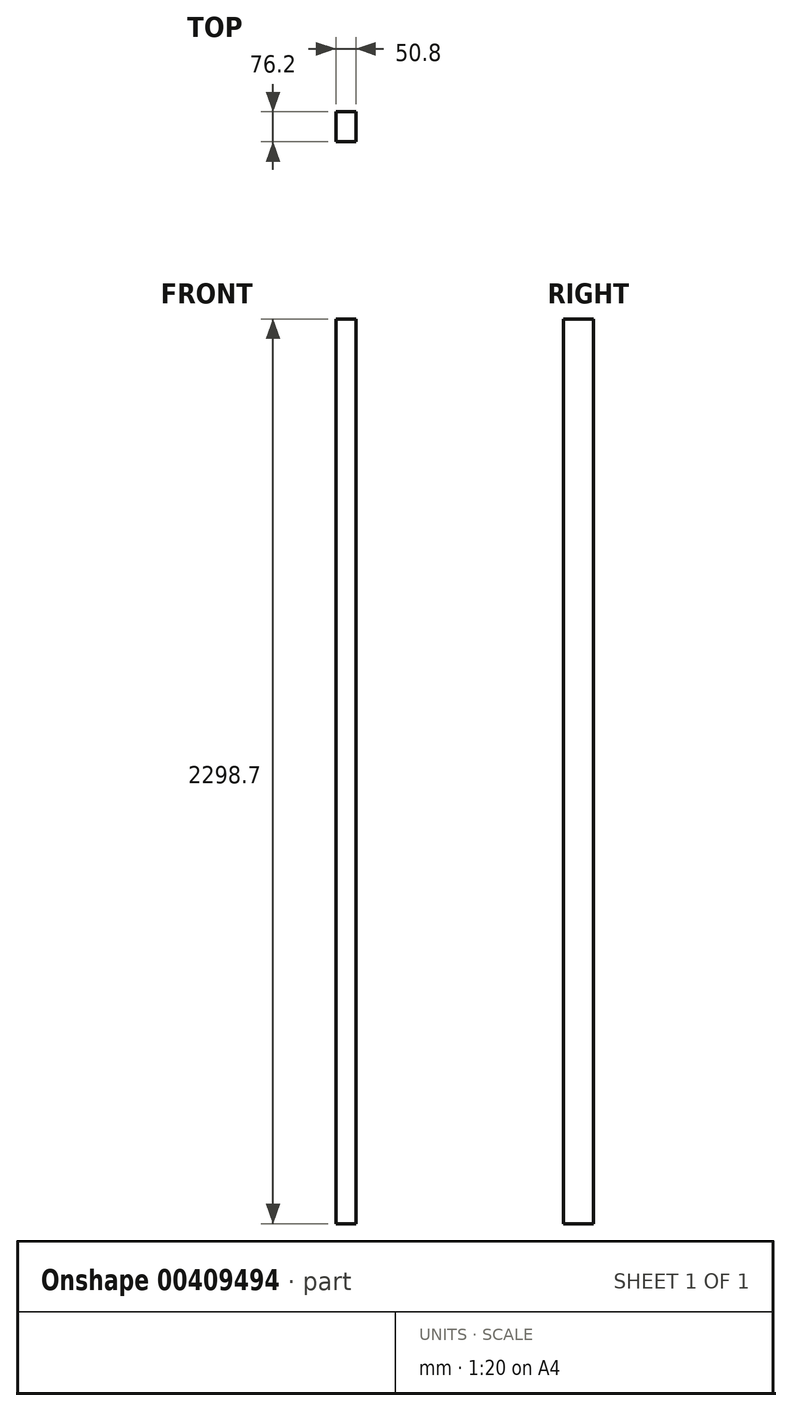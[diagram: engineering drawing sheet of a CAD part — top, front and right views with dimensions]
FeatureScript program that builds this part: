
annotation { "Feature Type Name" : "Feature", "Feature Type Description" : "" }
export const myFeature = defineFeature(function(context is Context, id is Id, definition is map)
    precondition{}
    {
        {
            var Q0;
            Q0=qCreatedBy(makeId("Front.planeOp"),FACE);
            var sketch = newSketch(context, id + "F0", { "sketchPlane" : qUnion([Q0])});
            skLineSegment(sketch, "E0.bottom", {"start": v(-25.4, 1149.35) * mm, "end": v(25.4, 1149.35) * mm});
            skLineSegment(sketch, "E0.top", {"start": v(-25.4, -1149.35) * mm, "end": v(25.4, -1149.35) * mm});
            skLineSegment(sketch, "E0.left", {"start": v(-25.4, 1149.35) * mm, "end": v(-25.4, -1149.35) * mm});
            skLineSegment(sketch, "E0.right", {"start": v(25.4, 1149.35) * mm, "end": v(25.4, -1149.35) * mm});
            skSolve(sketch);
        }
        {
            var Q0;
            Q0=makeQuery(id+"F0.imprint","IMPRINT",FACE,{"disambiguationData":[TD([[makeQuery(id+"F0.imprint","IMPRINT",EDGE,{"derivedFrom":sQuery(id+"F0.wireOp",EDGE,"E0.bottom")}),-1.0]])]});
            extrude(context, id + "F1", {"entities" : qUnion([Q0]), "depth" : 76.2 * mm});
        }
    });
